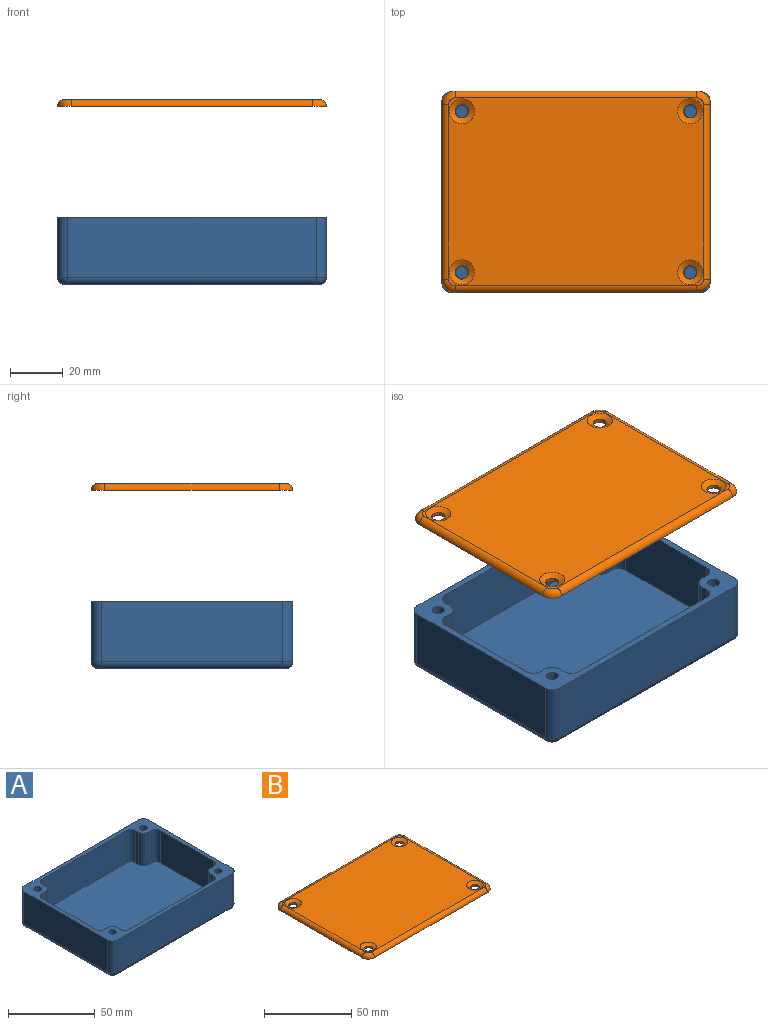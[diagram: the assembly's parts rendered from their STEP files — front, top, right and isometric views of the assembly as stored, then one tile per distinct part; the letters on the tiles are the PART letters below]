
ASSEMBLY  parts=2 mates=1
PART A: 51 faces, bbox 101.6x76.2x25.4 mm
  f0: plane 101.6x76.2mm, normal (0,0,1), area 1224.6mm2, adj f2,f3,f4,f5,f6,f7,f8,f9
  f1: plane 96.52x71.12mm, normal (0,0,1), area 6439.1mm2, adj f2,f3,f4,f5,f11,f12,f13,f14
  f2: plane 43.18x22.86mm, normal (-1,0,0), area 987.1mm2, adj f0,f1,f29,f35
  f3: plane 68.58x22.86mm, normal (0,1,0), area 1567.7mm2, adj f0,f1,f27,f32
  f4: plane 43.18x22.86mm, normal (1,0,0), area 987.1mm2, adj f0,f1,f30,f37
  f5: plane 68.58x22.86mm, normal (0,-1,0), area 1567.7mm2, adj f0,f1,f33,f38
  f6: plane 93.98x22.86mm, normal (0,-1,0), area 2148.4mm2, adj f0,f39,f42,f47
  f7: plane 68.58x22.86mm, normal (1,0,0), area 1567.7mm2, adj f0,f39,f40,f50
  f8: plane 93.98x22.86mm, normal (0,1,0), area 2148.4mm2, adj f0,f40,f41,f46
  f9: plane 68.58x22.86mm, normal (-1,0,0), area 1567.7mm2, adj f0,f41,f42,f43
  f10: plane 96.52x71.12mm, normal (0,0,-1), area 6863.1mm2, adj f43,f44,f45,f46,f47,f48,f49,f50
  f11: plane 22.86x2.54mm, normal (1,0,0), area 58.1mm2, adj f0,f1,f36,f38
  f12: plane 22.86x2.54mm, normal (0,-1,0), area 58.1mm2, adj f0,f1,f36,f37
  f13: plane 22.86x2.54mm, normal (-1,0,0), area 58.1mm2, adj f0,f1,f33,f34
  f14: plane 22.86x2.54mm, normal (0,-1,0), area 58.1mm2, adj f0,f1,f34,f35
  f15: plane 22.86x2.54mm, normal (1,0,0), area 58.1mm2, adj f0,f1,f31,f32
  f16: plane 22.86x2.54mm, normal (0,1,0), area 58.1mm2, adj f0,f1,f30,f31
  f17: plane 22.86x2.54mm, normal (0,1,0), area 58.1mm2, adj f0,f1,f28,f29
  f18: plane 22.86x2.54mm, normal (-1,0,0), area 58.1mm2, adj f0,f1,f27,f28
  f19: cylinder r=2.29mm len=12.7mm, axis (0,0,1), area 182.6mm2, adj f0,f20
  f20: plane 4.58x4.58mm, normal (0,0,1), area 16.4mm2, adj f19
  f21: cylinder r=2.29mm len=12.7mm, axis (0,0,1), area 182.6mm2, adj f0,f22
  f22: plane 4.58x4.58mm, normal (0,0,1), area 16.4mm2, adj f21
  f23: cylinder r=2.29mm len=12.7mm, axis (0,0,1), area 182.6mm2, adj f0,f24
  f24: plane 4.58x4.58mm, normal (0,0,1), area 16.4mm2, adj f23
  f25: cylinder r=2.29mm len=12.7mm, axis (0,0,1), area 182.6mm2, adj f0,f26
  f26: plane 4.58x4.58mm, normal (0,0,1), area 16.4mm2, adj f25
  f27: cylinder r=3.81mm len=22.86mm, axis (0,0,-1), area 136.8mm2, adj f0,f1,f3,f18
  f28: cylinder r=3.81mm len=22.86mm, axis (0,0,1), area 136.8mm2, adj f0,f1,f17,f18
  f29: cylinder r=3.81mm len=22.86mm, axis (0,0,1), area 136.8mm2, adj f0,f1,f2,f17
  f30: cylinder r=3.81mm len=22.86mm, axis (0,0,1), area 136.8mm2, adj f0,f1,f4,f16
  f31: cylinder r=3.81mm len=22.86mm, axis (0,0,1), area 136.8mm2, adj f0,f1,f15,f16
  f32: cylinder r=3.81mm len=22.86mm, axis (0,0,1), area 136.8mm2, adj f0,f1,f3,f15
  f33: cylinder r=3.81mm len=22.86mm, axis (0,0,-1), area 136.8mm2, adj f0,f1,f5,f13
  f34: cylinder r=3.81mm len=22.86mm, axis (0,0,1), area 136.8mm2, adj f0,f1,f13,f14
  f35: cylinder r=3.81mm len=22.86mm, axis (0,0,-1), area 136.8mm2, adj f0,f1,f2,f14
  f36: cylinder r=3.81mm len=22.86mm, axis (0,0,1), area 136.8mm2, adj f0,f1,f11,f12
  f37: cylinder r=3.81mm len=22.86mm, axis (0,0,-1), area 136.8mm2, adj f0,f1,f4,f12
  f38: cylinder r=3.81mm len=22.86mm, axis (0,0,1), area 136.8mm2, adj f0,f1,f5,f11
  f39: cylinder r=3.81mm len=22.86mm, axis (0,0,-1), area 136.8mm2, adj f0,f6,f7,f49
  f40: cylinder r=3.81mm len=22.86mm, axis (0,0,1), area 136.8mm2, adj f0,f7,f8,f48
  f41: cylinder r=3.81mm len=22.86mm, axis (0,0,-1), area 136.8mm2, adj f0,f8,f9,f44
  f42: cylinder r=3.81mm len=22.86mm, axis (0,0,1), area 136.8mm2, adj f0,f6,f9,f45
  f43: cylinder r=2.54mm len=68.58mm, axis (0,-1,0), area 273.6mm2, adj f9,f10,f44,f45
  f44: torus R=1.27mm, axis (0,0,1), area 18.1mm2, adj f10,f41,f43,f46
  f45: torus R=1.27mm, axis (0,0,1), area 18.1mm2, adj f10,f42,f43,f47
  f46: cylinder r=2.54mm len=93.98mm, axis (-1,0,0), area 375mm2, adj f8,f10,f44,f48
  f47: cylinder r=2.54mm len=93.98mm, axis (1,0,0), area 375mm2, adj f6,f10,f45,f49
  f48: torus R=1.27mm, axis (0,0,1), area 18.1mm2, adj f10,f40,f46,f50
  f49: torus R=1.27mm, axis (0,0,1), area 18.1mm2, adj f10,f39,f47,f50
  f50: cylinder r=2.54mm len=68.58mm, axis (0,1,0), area 273.6mm2, adj f7,f10,f48,f49
PART B: 18 faces, bbox 102.4x77x2.5 mm
  f0: plane 96.52x71.12mm, normal (0,0,1), area 6576.7mm2, adj f6,f7,f8,f9,f10,f11,f12,f13
  f1: plane 101.6x76.2mm, normal (0,0,-1), area 7638.7mm2, adj f2,f3,f4,f5,f10,f11,f12,f13
  f2: cylinder r=2.54mm len=5.08mm, axis (0,0,1), area 20.3mm2, adj f1,f8
  f3: cylinder r=2.54mm len=5.08mm, axis (0,0,1), area 20.3mm2, adj f1,f7
  f4: cylinder r=2.54mm len=5.08mm, axis (0,0,1), area 20.3mm2, adj f1,f6
  f5: cylinder r=2.54mm len=5.08mm, axis (0,0,1), area 20.3mm2, adj f1,f9
  f6: cone r=4.74mm half-angle=60deg, axis (0,0,1), area 58.1mm2, adj f0,f4
  f7: cone r=2.54mm half-angle=60deg, axis (0,0,1), area 58.1mm2, adj f0,f3
  f8: cone r=4.74mm half-angle=60deg, axis (0,0,1), area 58.1mm2, adj f0,f2
  f9: cone r=2.54mm half-angle=60deg, axis (0,0,1), area 58.1mm2, adj f0,f5
  f10: cylinder r=2.54mm len=91.44mm, axis (-1,0,0), area 364.8mm2, adj f0,f1,f11,f12
  f11: torus R=2.54mm, axis (0,0,1), area 26.1mm2, adj f0,f1,f10,f13
  f12: torus R=2.54mm, axis (0,0,1), area 26.1mm2, adj f0,f1,f10,f14
  f13: cylinder r=2.54mm len=66.04mm, axis (0,-1,0), area 263.5mm2, adj f0,f1,f11,f15
  f14: cylinder r=2.54mm len=66.04mm, axis (0,1,0), area 263.5mm2, adj f0,f1,f12,f16
  f15: torus R=2.54mm, axis (0,0,1), area 26.1mm2, adj f0,f1,f13,f17
  f16: torus R=2.54mm, axis (0,0,1), area 26.1mm2, adj f0,f1,f14,f17
  f17: cylinder r=2.54mm len=91.44mm, axis (1,0,0), area 364.8mm2, adj f0,f1,f15,f16
PLACE A t=(-41.67,-12.1,-8.74)mm fixed
PLACE B t=(80.95,-14.77,58.74)mm
MATE slider A.f19 <-> B.f5  axis (0,0,1) through (-84.85,18.38,16.66)mm
